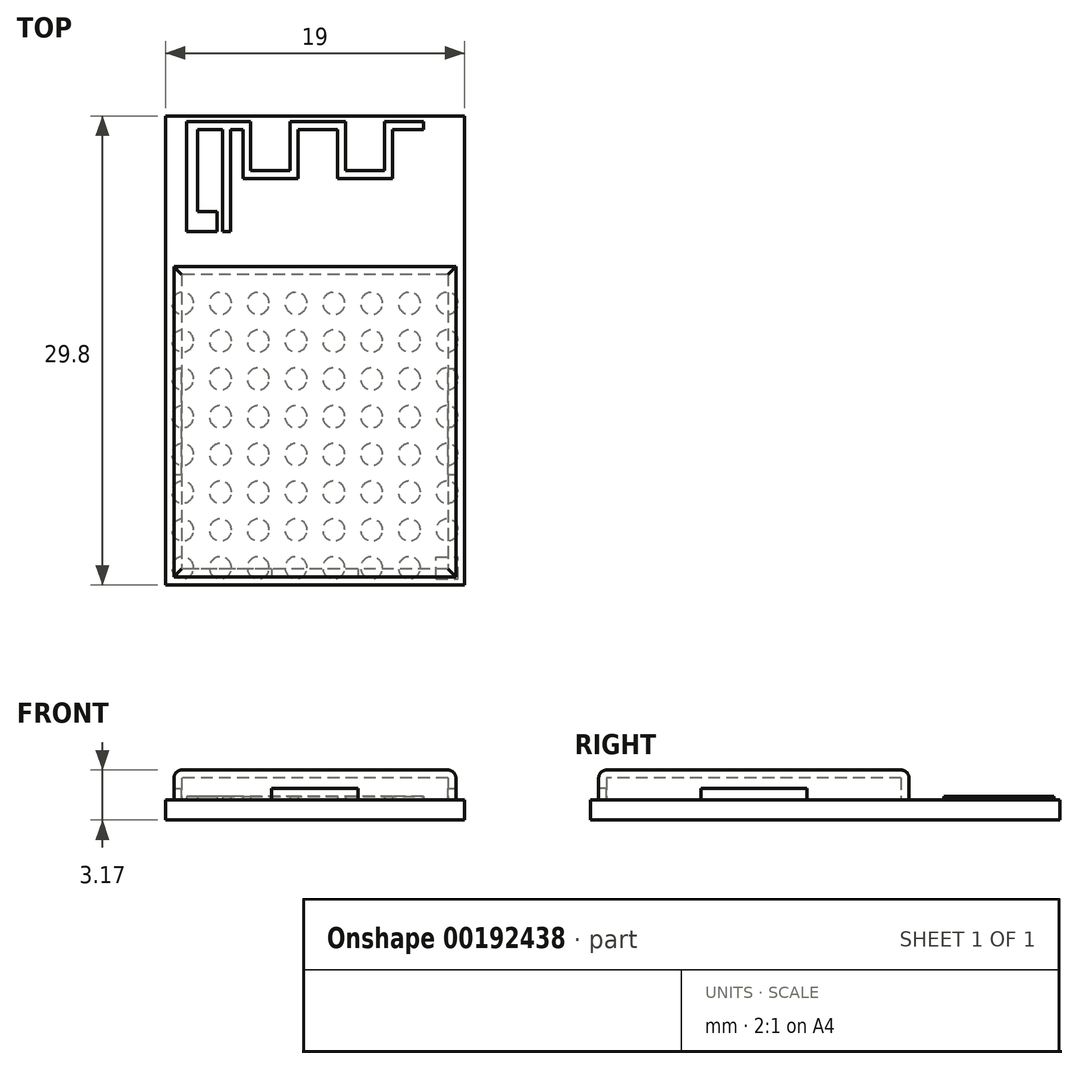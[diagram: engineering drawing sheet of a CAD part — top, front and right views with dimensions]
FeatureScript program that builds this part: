
annotation { "Feature Type Name" : "Feature", "Feature Type Description" : "" }
export const myFeature = defineFeature(function(context is Context, id is Id, definition is map)
    precondition{}
    {
        {
            var Q0;
            Q0=qCreatedBy(makeId("Top.planeOp"),FACE);
            var sketch = newSketch(context, id + "F0", { "sketchPlane" : qUnion([Q0])});
            skLineSegment(sketch, "E0.bottom", {"start": v(9.5, -14.9) * mm, "end": v(-9.5, -14.9) * mm});
            skLineSegment(sketch, "E0.top", {"start": v(9.5, 14.9) * mm, "end": v(-9.5, 14.9) * mm});
            skLineSegment(sketch, "E0.left", {"start": v(9.5, -14.9) * mm, "end": v(9.5, 14.9) * mm});
            skLineSegment(sketch, "E0.right", {"start": v(-9.5, -14.9) * mm, "end": v(-9.5, 14.9) * mm});
            skPoint(sketch, "E0.middle", {"position": v(0, 0) * mm});
            skSolve(sketch);
        }
        {
            var Q0;
            Q0 = qSketchRegion(id + "F0", true);
            extrude(context, id + "F1", {"entities" : qUnion([Q0]), "depth" : 1.27 * mm});
        }
        {
            var Q0;
            Q0=makeQuery(id+"F1.opExtrude","CAP_FACE",FACE,{"disambiguationData":[OSD([sQuery(id+"F0.wireOp",EDGE,"E0.bottom"),sQuery(id+"F0.wireOp",EDGE,"E0.top"),sQuery(id+"F0.wireOp",EDGE,"E0.left"),sQuery(id+"F0.wireOp",EDGE,"E0.right")])],"isStart":false});
            var sketch = newSketch(context, id + "F2", { "sketchPlane" : qUnion([Q0])});
            skLineSegment(sketch, "E1.bottom", {"start": v(-8.96, 5.33) * mm, "end": v(8.96, 5.33) * mm});
            skLineSegment(sketch, "E1.top", {"start": v(-8.95, -14.38) * mm, "end": v(8.96, -14.38) * mm});
            skLineSegment(sketch, "E1.left", {"start": v(-8.96, 5.33) * mm, "end": v(-8.96, -14.38) * mm});
            skLineSegment(sketch, "E1.right", {"start": v(8.95, 5.33) * mm, "end": v(8.95, -14.38) * mm});
            skCircle(sketch, "E2", {"center": v(8, 7.4) * mm, "radius": 1 * mm});
            skSolve(sketch);
        }
        {
            var Q0;
            Q0=makeQuery(id+"F2.imprint","IMPRINT",FACE,{"disambiguationData":[TD([[makeQuery(id+"F2.imprint","IMPRINT",EDGE,{"derivedFrom":sQuery(id+"F2.wireOp",EDGE,"E1.bottom")}),-1.0]])]});
            extrude(context, id + "F3", {"entities" : qUnion([Q0]), "depth" : 1.88 * mm});
        }
        {
            var Q0;
            Q0=makeQuery(id+"F2.imprint","IMPRINT",FACE,{"disambiguationData":[TD([[makeQuery(id+"F2.imprint","IMPRINT",EDGE,{"derivedFrom":sQuery(id+"F2.wireOp",EDGE,"E2")}),1.0]])]});
            extrude(context, id + "F4", {"entities" : qUnion([Q0]), "depth" : 1.25 * mm});
        }
        {
            var Q0;
            Q0=makeQuery(id+"F3.opExtrude","CAP_FACE",FACE,{"disambiguationData":[OSD([sQuery(id+"F2.wireOp",EDGE,"E1.bottom"),sQuery(id+"F2.wireOp",EDGE,"E1.top"),sQuery(id+"F2.wireOp",EDGE,"E1.left"),sQuery(id+"F2.wireOp",EDGE,"E1.right")])],"isStart":true});
            var sketch = newSketch(context, id + "F5", { "sketchPlane" : qUnion([Q0])});
            skLineSegment(sketch, "E3.bottom", {"start": v(8.45, -4.83) * mm, "end": v(-8.45, -4.83) * mm});
            skLineSegment(sketch, "E3.top", {"start": v(8.45, 13.88) * mm, "end": v(-8.46, 13.88) * mm});
            skLineSegment(sketch, "E3.left", {"start": v(8.45, -4.83) * mm, "end": v(8.45, 13.88) * mm});
            skLineSegment(sketch, "E3.right", {"start": v(-8.45, -4.83) * mm, "end": v(-8.46, 13.88) * mm});
            skSolve(sketch);
        }
        {
            var Q0;
            Q0 = qSketchRegion(id + "F5", true);
            extrude(context, id + "F6", {"entities" : qUnion([Q0]), "operationType" : NewBodyOperationType.REMOVE, "oppositeDirection" : true, "depth" : 1.38 * mm});
        }
        {
            var Q0;
            Q0=makeQuery(id+"F3.opExtrude","SWEPT_FACE",FACE,{"disambiguationData":[OSD([sQuery(id+"F2.wireOp",EDGE,"E1.top")])]});
            var sketch = newSketch(context, id + "F7", { "sketchPlane" : qUnion([Q0])});
            skLineSegment(sketch, "E4.top", {"start": v(2.75, 1.97) * mm, "end": v(-2.75, 1.97) * mm});
            skLineSegment(sketch, "E4.left", {"start": v(2.75, 1.27) * mm, "end": v(2.75, 1.97) * mm});
            skLineSegment(sketch, "E4.right", {"start": v(-2.75, 1.27) * mm, "end": v(-2.75, 1.97) * mm});
            skPoint(sketch, "E4.middle", {"position": v(0, 1.27) * mm});
            skLineSegment(sketch, "E5", {"start": v(0, 1.27) * mm, "end": v(2.75, 1.27) * mm});
            skLineSegment(sketch, "E6", {"start": v(0, 1.27) * mm, "end": v(-2.76, 1.27) * mm});
            skPoint(sketch, "E7.orphan", {"position": v(-2.75, 0.57) * mm});
            skPoint(sketch, "E8.orphan", {"position": v(2.75, 0.57) * mm});
            skSolve(sketch);
        }
        {
            var Q0;
            Q0=makeQuery(id+"F7.imprint","IMPRINT",FACE,{"disambiguationData":[TD([[makeQuery(id+"F7.imprint","IMPRINT",EDGE,{"derivedFrom":sQuery(id+"F7.wireOp",EDGE,"E4.top")}),1.0]])]});
            extrude(context, id + "F8", {"entities" : qUnion([Q0]), "operationType" : NewBodyOperationType.REMOVE, "oppositeDirection" : true, "depth" : .5 * mm});
        }
        {
            var Q0;
            Q0=makeQuery(id+"F3.opExtrude","SWEPT_FACE",FACE,{"disambiguationData":[OSD([sQuery(id+"F2.wireOp",EDGE,"E1.right")])]});
            var sketch = newSketch(context, id + "F9", { "sketchPlane" : qUnion([Q0])});
            skLineSegment(sketch, "E9.bottom", {"start": v(-1.16, 1.27) * mm, "end": v(-7.89, 1.27) * mm});
            skLineSegment(sketch, "E9.left", {"start": v(-1.16, 1.27) * mm, "end": v(-1.16, 1.97) * mm});
            skLineSegment(sketch, "E9.right", {"start": v(-7.89, 1.27) * mm, "end": v(-7.89, 1.97) * mm});
            skPoint(sketch, "E9.middle", {"position": v(-4.52, 3.15) * mm});
            skLineSegment(sketch, "E10", {"start": v(-7.89, 1.97) * mm, "end": v(-1.16, 1.97) * mm});
            skPoint(sketch, "E11.orphan", {"position": v(-7.89, 5.03) * mm});
            skPoint(sketch, "E12.orphan", {"position": v(-1.16, 5.03) * mm});
            skLineSegment(sketch, "E13", {"start": v(-7.89, 1.27) * mm, "end": v(-1.16, 1.27) * mm});
            skSolve(sketch);
        }
        {
            var Q0;
            Q0=makeQuery(id+"F9.imprint","IMPRINT",FACE,{"disambiguationData":[TD([[makeQuery(id+"F9.imprint","IMPRINT",EDGE,{"derivedFrom":sQuery(id+"F9.wireOp",EDGE,"E9.left")}),1.0]])]});
            extrude(context, id + "F10", {"entities" : qUnion([Q0]), "operationType" : NewBodyOperationType.REMOVE, "endBound" : BoundingType.THROUGH_ALL, "oppositeDirection" : true, "depth" : 25 * mm});
        }
        {
            var Q0;
            Q0=makeQuery(id+"F4.opExtrude","SWEPT_BODY",BODY,{"disambiguationData":[OSD([sQuery(id+"F2.wireOp",EDGE,"E2")])]});
            deleteBodies(context, id + "F11", {"entities" : qUnion([Q0])});
        }
        {
            var Q0;
            Q0=makeQuery(id+"F1.opExtrude","CAP_FACE",FACE,{"disambiguationData":[OSD([sQuery(id+"F0.wireOp",EDGE,"E0.bottom"),sQuery(id+"F0.wireOp",EDGE,"E0.top"),sQuery(id+"F0.wireOp",EDGE,"E0.left"),sQuery(id+"F0.wireOp",EDGE,"E0.right")])],"isStart":true});
            var sketch = newSketch(context, id + "F12", { "sketchPlane" : qUnion([Q0])});
            skCircle(sketch, "E14", {"center": v(8.4, 13.8) * mm, "radius": 0.7 * mm});
            skCircle(sketch, "E15.1.0.0", {"center": v(6, 13.8) * mm, "radius": 0.7 * mm});
            skCircle(sketch, "E15.2.0.0", {"center": v(3.6, 13.8) * mm, "radius": 0.7 * mm});
            skCircle(sketch, "E15.3.0.0", {"center": v(1.2, 13.8) * mm, "radius": 0.7 * mm});
            skCircle(sketch, "E15.4.0.0", {"center": v(-1.2, 13.8) * mm, "radius": 0.7 * mm});
            skCircle(sketch, "E15.5.0.0", {"center": v(-3.6, 13.8) * mm, "radius": 0.7 * mm});
            skCircle(sketch, "E15.6.0.0", {"center": v(-6, 13.8) * mm, "radius": 0.7 * mm});
            skCircle(sketch, "E15.7.0.0", {"center": v(-8.4, 13.8) * mm, "radius": 0.7 * mm});
            skLineSegment(sketch, "E15.direction1", {"start": v(8.4, 13.8) * mm, "end": v(6, 13.8) * mm, "construction": true});
            skCircle(sketch, "E16.1.0.0", {"center": v(8.4, 11.4) * mm, "radius": 0.7 * mm});
            skCircle(sketch, "E16.1.0.1", {"center": v(6, 11.4) * mm, "radius": 0.7 * mm});
            skCircle(sketch, "E16.1.0.2", {"center": v(3.6, 11.4) * mm, "radius": 0.7 * mm});
            skCircle(sketch, "E16.1.0.3", {"center": v(1.2, 11.4) * mm, "radius": 0.7 * mm});
            skCircle(sketch, "E16.1.0.4", {"center": v(-1.2, 11.4) * mm, "radius": 0.7 * mm});
            skCircle(sketch, "E16.1.0.5", {"center": v(-3.6, 11.4) * mm, "radius": 0.7 * mm});
            skCircle(sketch, "E16.1.0.6", {"center": v(-6, 11.4) * mm, "radius": 0.7 * mm});
            skCircle(sketch, "E16.1.0.7", {"center": v(-8.4, 11.4) * mm, "radius": 0.7 * mm});
            skCircle(sketch, "E16.2.0.0", {"center": v(8.4, 9) * mm, "radius": 0.7 * mm});
            skCircle(sketch, "E16.2.0.1", {"center": v(6, 9) * mm, "radius": 0.7 * mm});
            skCircle(sketch, "E16.2.0.2", {"center": v(3.6, 9) * mm, "radius": 0.7 * mm});
            skCircle(sketch, "E16.2.0.3", {"center": v(1.2, 9) * mm, "radius": 0.7 * mm});
            skCircle(sketch, "E16.2.0.4", {"center": v(-1.2, 9) * mm, "radius": 0.7 * mm});
            skCircle(sketch, "E16.2.0.5", {"center": v(-3.6, 9) * mm, "radius": 0.7 * mm});
            skCircle(sketch, "E16.2.0.6", {"center": v(-6, 9) * mm, "radius": 0.7 * mm});
            skCircle(sketch, "E16.2.0.7", {"center": v(-8.4, 9) * mm, "radius": 0.7 * mm});
            skCircle(sketch, "E16.3.0.0", {"center": v(8.4, 6.6) * mm, "radius": 0.7 * mm});
            skCircle(sketch, "E16.3.0.1", {"center": v(6, 6.6) * mm, "radius": 0.7 * mm});
            skCircle(sketch, "E16.3.0.2", {"center": v(3.6, 6.6) * mm, "radius": 0.7 * mm});
            skCircle(sketch, "E16.3.0.3", {"center": v(1.2, 6.6) * mm, "radius": 0.7 * mm});
            skCircle(sketch, "E16.3.0.4", {"center": v(-1.2, 6.6) * mm, "radius": 0.7 * mm});
            skCircle(sketch, "E16.3.0.5", {"center": v(-3.6, 6.6) * mm, "radius": 0.7 * mm});
            skCircle(sketch, "E16.3.0.6", {"center": v(-6, 6.6) * mm, "radius": 0.7 * mm});
            skCircle(sketch, "E16.3.0.7", {"center": v(-8.4, 6.6) * mm, "radius": 0.7 * mm});
            skCircle(sketch, "E16.4.0.0", {"center": v(8.4, 4.2) * mm, "radius": 0.7 * mm});
            skCircle(sketch, "E16.4.0.1", {"center": v(6, 4.2) * mm, "radius": 0.7 * mm});
            skCircle(sketch, "E16.4.0.2", {"center": v(3.6, 4.2) * mm, "radius": 0.7 * mm});
            skCircle(sketch, "E16.4.0.3", {"center": v(1.2, 4.2) * mm, "radius": 0.7 * mm});
            skCircle(sketch, "E16.4.0.4", {"center": v(-1.2, 4.2) * mm, "radius": 0.7 * mm});
            skCircle(sketch, "E16.4.0.5", {"center": v(-3.6, 4.2) * mm, "radius": 0.7 * mm});
            skCircle(sketch, "E16.4.0.6", {"center": v(-6, 4.2) * mm, "radius": 0.7 * mm});
            skCircle(sketch, "E16.4.0.7", {"center": v(-8.4, 4.2) * mm, "radius": 0.7 * mm});
            skCircle(sketch, "E16.5.0.0", {"center": v(8.4, 1.8) * mm, "radius": 0.7 * mm});
            skCircle(sketch, "E16.5.0.1", {"center": v(6, 1.8) * mm, "radius": 0.7 * mm});
            skCircle(sketch, "E16.5.0.2", {"center": v(3.6, 1.8) * mm, "radius": 0.7 * mm});
            skCircle(sketch, "E16.5.0.3", {"center": v(1.2, 1.8) * mm, "radius": 0.7 * mm});
            skCircle(sketch, "E16.5.0.4", {"center": v(-1.2, 1.8) * mm, "radius": 0.7 * mm});
            skCircle(sketch, "E16.5.0.5", {"center": v(-3.6, 1.8) * mm, "radius": 0.7 * mm});
            skCircle(sketch, "E16.5.0.6", {"center": v(-6, 1.8) * mm, "radius": 0.7 * mm});
            skCircle(sketch, "E16.5.0.7", {"center": v(-8.4, 1.8) * mm, "radius": 0.7 * mm});
            skCircle(sketch, "E16.6.0.0", {"center": v(8.4, -0.6) * mm, "radius": 0.7 * mm});
            skCircle(sketch, "E16.6.0.1", {"center": v(6, -0.6) * mm, "radius": 0.7 * mm});
            skCircle(sketch, "E16.6.0.2", {"center": v(3.6, -0.6) * mm, "radius": 0.7 * mm});
            skCircle(sketch, "E16.6.0.3", {"center": v(1.2, -0.6) * mm, "radius": 0.7 * mm});
            skCircle(sketch, "E16.6.0.4", {"center": v(-1.2, -0.6) * mm, "radius": 0.7 * mm});
            skCircle(sketch, "E16.6.0.5", {"center": v(-3.6, -0.6) * mm, "radius": 0.7 * mm});
            skCircle(sketch, "E16.6.0.6", {"center": v(-6, -0.6) * mm, "radius": 0.7 * mm});
            skCircle(sketch, "E16.6.0.7", {"center": v(-8.4, -0.6) * mm, "radius": 0.7 * mm});
            skCircle(sketch, "E16.7.0.0", {"center": v(8.4, -3) * mm, "radius": 0.7 * mm});
            skCircle(sketch, "E16.7.0.1", {"center": v(6, -3) * mm, "radius": 0.7 * mm});
            skCircle(sketch, "E16.7.0.2", {"center": v(3.6, -3) * mm, "radius": 0.7 * mm});
            skCircle(sketch, "E16.7.0.3", {"center": v(1.2, -3) * mm, "radius": 0.7 * mm});
            skCircle(sketch, "E16.7.0.4", {"center": v(-1.2, -3) * mm, "radius": 0.7 * mm});
            skCircle(sketch, "E16.7.0.5", {"center": v(-3.6, -3) * mm, "radius": 0.7 * mm});
            skCircle(sketch, "E16.7.0.6", {"center": v(-6, -3) * mm, "radius": 0.7 * mm});
            skCircle(sketch, "E16.7.0.7", {"center": v(-8.4, -3) * mm, "radius": 0.7 * mm});
            skLineSegment(sketch, "E16.direction1", {"start": v(8.4, 13.8) * mm, "end": v(8.4, 11.4) * mm, "construction": true});
            skLineSegment(sketch, "E17.bottom", {"start": v(7.7, 14.5) * mm, "end": v(9.1, 14.5) * mm});
            skLineSegment(sketch, "E17.top", {"start": v(7.7, 13.1) * mm, "end": v(9.1, 13.1) * mm});
            skLineSegment(sketch, "E17.left", {"start": v(7.7, 14.5) * mm, "end": v(7.7, 13.1) * mm});
            skLineSegment(sketch, "E17.right", {"start": v(9.1, 14.5) * mm, "end": v(9.1, 13.1) * mm});
            skSolve(sketch);
        }
        {
            var Q0;
            Q0 = qSketchRegion(id + "F12", true);
            extrude(context, id + "F13", {"entities" : qUnion([Q0]), "depth" : 0.02 * mm});
        }
        {
            var Q0;
            Q0=makeQuery(id+"F1.opExtrude","CAP_FACE",FACE,{"disambiguationData":[OSD([sQuery(id+"F0.wireOp",EDGE,"E0.bottom"),sQuery(id+"F0.wireOp",EDGE,"E0.top"),sQuery(id+"F0.wireOp",EDGE,"E0.left"),sQuery(id+"F0.wireOp",EDGE,"E0.right")])],"isStart":false});
            var sketch = newSketch(context, id + "F14", { "sketchPlane" : qUnion([Q0])});
            skLineSegment(sketch, "E18", {"start": v(-6.22, 7.56) * mm, "end": v(-8.14, 7.56) * mm});
            skLineSegment(sketch, "E19", {"start": v(-8.14, 7.56) * mm, "end": v(-8.14, 14.53) * mm});
            skLineSegment(sketch, "E20", {"start": v(-8.14, 14.53) * mm, "end": v(-4.08, 14.53) * mm});
            skLineSegment(sketch, "E21", {"start": v(-4.08, 14.53) * mm, "end": v(-4.08, 11.43) * mm});
            skLineSegment(sketch, "E22", {"start": v(-4.08, 11.43) * mm, "end": v(-1.58, 11.43) * mm});
            skLineSegment(sketch, "E23", {"start": v(-1.58, 11.43) * mm, "end": v(-1.58, 14.53) * mm});
            skLineSegment(sketch, "E24", {"start": v(-1.58, 14.53) * mm, "end": v(1.93, 14.53) * mm});
            skLineSegment(sketch, "E25", {"start": v(1.93, 11.43) * mm, "end": v(4.43, 11.43) * mm});
            skLineSegment(sketch, "E26", {"start": v(4.43, 11.43) * mm, "end": v(4.43, 14.53) * mm});
            skLineSegment(sketch, "E27", {"start": v(4.43, 14.53) * mm, "end": v(6.9, 14.53) * mm});
            skLineSegment(sketch, "E28", {"start": v(6.9, 14.53) * mm, "end": v(6.9, 14.03) * mm});
            skLineSegment(sketch, "E29", {"start": v(6.9, 14.03) * mm, "end": v(4.93, 14.03) * mm});
            skLineSegment(sketch, "E30", {"start": v(4.93, 14.03) * mm, "end": v(4.93, 10.93) * mm});
            skLineSegment(sketch, "E31", {"start": v(4.93, 10.93) * mm, "end": v(1.43, 10.93) * mm});
            skLineSegment(sketch, "E32", {"start": v(1.43, 14.03) * mm, "end": v(-1.08, 14.03) * mm});
            skLineSegment(sketch, "E33", {"start": v(-1.08, 14.03) * mm, "end": v(-1.08, 10.93) * mm});
            skLineSegment(sketch, "E34", {"start": v(-1.08, 10.93) * mm, "end": v(-4.58, 10.93) * mm});
            skLineSegment(sketch, "E35", {"start": v(-4.58, 10.93) * mm, "end": v(-4.58, 14.03) * mm});
            skLineSegment(sketch, "E36", {"start": v(-4.58, 14.03) * mm, "end": v(-7.44, 14.03) * mm});
            skLineSegment(sketch, "E37", {"start": v(-7.44, 14.03) * mm, "end": v(-7.44, 8.81) * mm});
            skLineSegment(sketch, "E38", {"start": v(-7.44, 8.81) * mm, "end": v(-6.22, 8.81) * mm});
            skLineSegment(sketch, "E39", {"start": v(-6.22, 8.81) * mm, "end": v(-6.22, 7.56) * mm});
            skLineSegment(sketch, "E40", {"start": v(1.93, 14.53) * mm, "end": v(1.93, 11.43) * mm});
            skLineSegment(sketch, "E41", {"start": v(1.43, 14.03) * mm, "end": v(1.43, 10.93) * mm});
            skLineSegment(sketch, "E42", {"start": v(-5.87, 7.56) * mm, "end": v(-5.87, 14.03) * mm});
            skLineSegment(sketch, "E43", {"start": v(-5.37, 14.03) * mm, "end": v(-5.37, 7.56) * mm});
            skLineSegment(sketch, "E44", {"start": v(-5.37, 7.56) * mm, "end": v(-5.87, 7.56) * mm});
            skPoint(sketch, "E45.orphan", {"position": v(0, 10.93) * mm});
            skSolve(sketch);
        }
        {
            var Q0;
            Q0 = qSketchRegion(id + "F14", true);
            extrude(context, id + "F15", {"entities" : qUnion([Q0]), "operationType" : NewBodyOperationType.ADD, "depth" : .20 * mm});
        }
        {
            var Q0;
            Q0=makeQuery(id+"F3.opExtrude","CAP_EDGE",EDGE,{"disambiguationData":[OSD([sQuery(id+"F2.wireOp",EDGE,"E1.left")])],"isStart":false});
            var Q1;
            Q1=makeQuery(id+"F3.opExtrude","CAP_EDGE",EDGE,{"disambiguationData":[OSD([sQuery(id+"F2.wireOp",EDGE,"E1.top")])],"isStart":false});
            var Q2;
            Q2=makeQuery(id+"F3.opExtrude","CAP_EDGE",EDGE,{"disambiguationData":[OSD([sQuery(id+"F2.wireOp",EDGE,"E1.right")])],"isStart":false});
            var Q3;
            Q3=makeQuery(id+"F3.opExtrude","CAP_EDGE",EDGE,{"disambiguationData":[OSD([sQuery(id+"F2.wireOp",EDGE,"E1.bottom")])],"isStart":false});
            fillet(context, id + "F16", {"entities" : qUnion([Q0, Q1, Q2, Q3]), "radius" : .5 * mm, "tangentPropagation" : true, "allowEdgeOverflow" : false});
        }
    });
